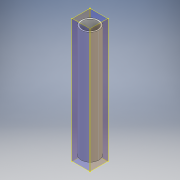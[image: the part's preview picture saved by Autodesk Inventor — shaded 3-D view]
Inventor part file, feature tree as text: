
AUTODESK INVENTOR PART (.ipt)
format: ipt  version: 2018 (Build 220112000, 112)  size: 98,816 bytes
history: native  units: mm
features: other x5, extrude x1, sketch x1
ambient origin geometry x8: Origin, YZ Plane, XZ Plane, XY Plane, X Axis, Y Axis, Z Axis, Center Point
bodies: Body1 (feature_tree)
feature tree (7):
  other  "ソリッド1"
  extrude  "押し出し1"  Depth=27.2mm
  other  "作業平面1"
  other  "作業平面3"
  other  "作業平面4"
  other  "作業平面5"
  sketch  "スケッチ1"
